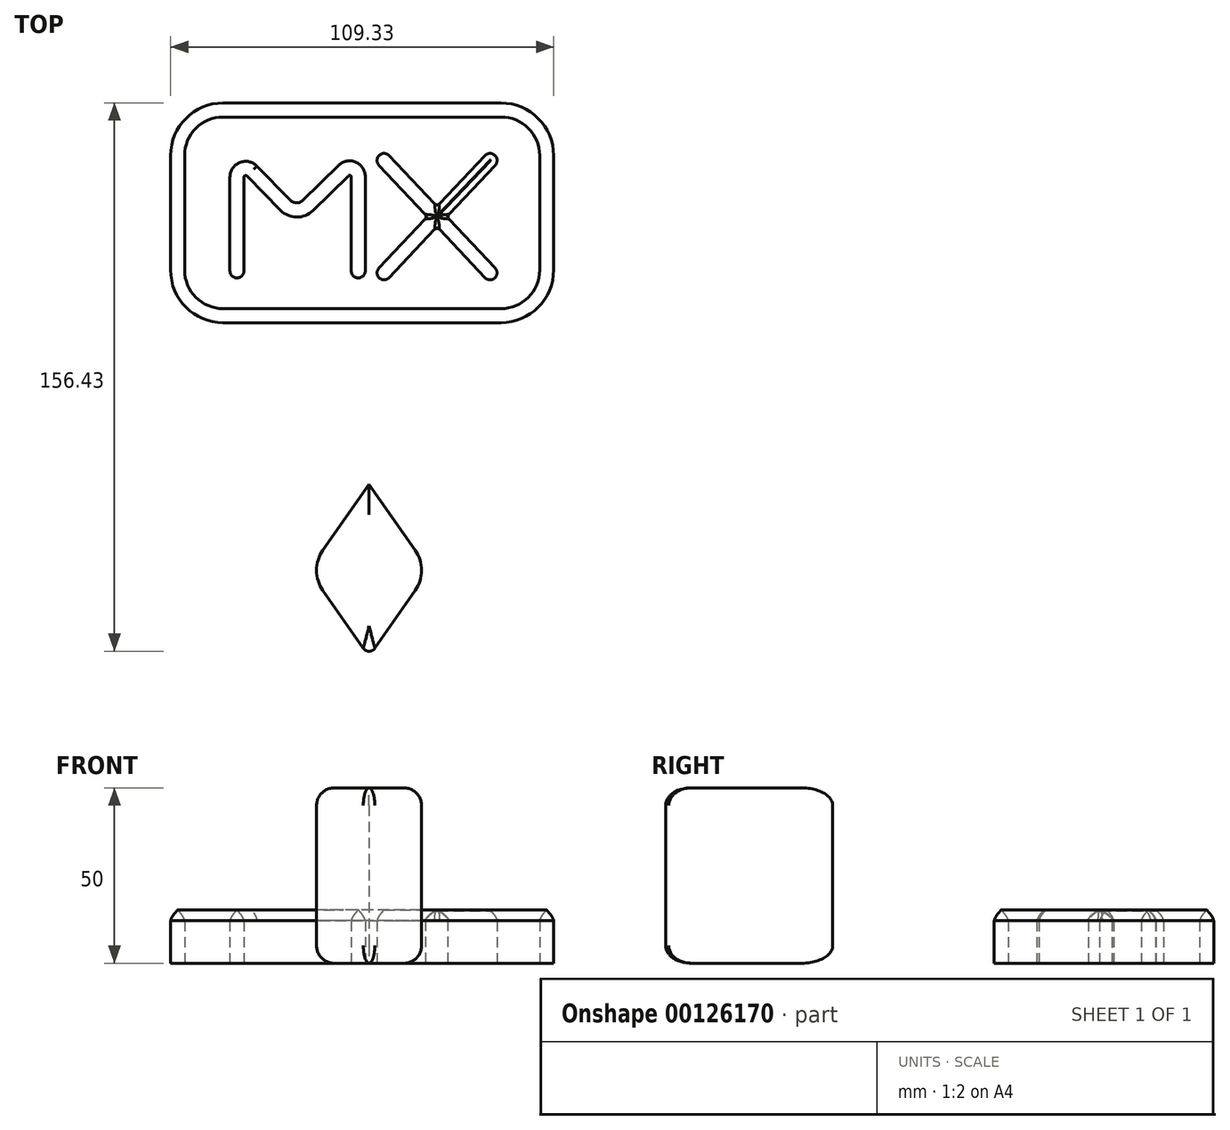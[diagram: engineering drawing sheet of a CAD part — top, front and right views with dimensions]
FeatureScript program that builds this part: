
annotation { "Feature Type Name" : "Feature", "Feature Type Description" : "" }
export const myFeature = defineFeature(function(context is Context, id is Id, definition is map)
    precondition{}
    {
        {
            var Q0;
            Q0=qCreatedBy(makeId("Top.planeOp"),FACE);
            var sketch = newSketch(context, id + "F0", { "sketchPlane" : qUnion([Q0])});
            skLineSegment(sketch, "E0.bottom", {"start": v(-41.65, 32.84) * mm, "end": v(37.68, 32.84) * mm});
            skLineSegment(sketch, "E0.top", {"start": v(-41.65, -29.83) * mm, "end": v(37.68, -29.83) * mm});
            skLineSegment(sketch, "E0.left", {"start": v(-56.65, 17.84) * mm, "end": v(-56.65, -14.83) * mm});
            skLineSegment(sketch, "E0.right", {"start": v(52.68, 17.84) * mm, "end": v(52.68, -14.83) * mm});
            skLineSegment(sketch, "E1.0", {"start": v(-41.65, 28.84) * mm, "end": v(37.68, 28.84) * mm});
            skLineSegment(sketch, "E1.1", {"start": v(-52.65, 17.84) * mm, "end": v(-52.65, -14.83) * mm});
            skLineSegment(sketch, "E1.2", {"start": v(-41.65, -25.83) * mm, "end": v(37.68, -25.83) * mm});
            skLineSegment(sketch, "E1.3", {"start": v(48.68, 17.84) * mm, "end": v(48.68, -14.83) * mm});
            skPoint(sketch, "E2.visualSharp", {"position": v(-56.65, 32.84) * mm});
            skArc(sketch, "E2.filletArc", {"start": v(-41.65, 32.84) * mm, "mid": v(-52.25, 28.45) * mm, "end": v(-56.65, 17.84) * mm});
            skPoint(sketch, "E3.visualSharp", {"position": v(-56.65, -29.83) * mm});
            skArc(sketch, "E3.filletArc", {"start": v(-56.65, -14.83) * mm, "mid": v(-52.25, -25.43) * mm, "end": v(-41.65, -29.83) * mm});
            skPoint(sketch, "E4.visualSharp", {"position": v(52.68, -29.83) * mm});
            skArc(sketch, "E4.filletArc", {"start": v(37.68, -29.83) * mm, "mid": v(48.28, -25.43) * mm, "end": v(52.68, -14.83) * mm});
            skPoint(sketch, "E5.visualSharp", {"position": v(52.68, 32.84) * mm});
            skArc(sketch, "E5.filletArc", {"start": v(52.68, 17.84) * mm, "mid": v(48.28, 28.45) * mm, "end": v(37.68, 32.84) * mm});
            skPoint(sketch, "E6.visualSharp", {"position": v(48.68, 28.84) * mm});
            skArc(sketch, "E6.filletArc", {"start": v(48.68, 17.84) * mm, "mid": v(45.45, 25.62) * mm, "end": v(37.68, 28.84) * mm});
            skPoint(sketch, "E7.visualSharp", {"position": v(48.68, -25.83) * mm});
            skArc(sketch, "E7.filletArc", {"start": v(37.68, -25.83) * mm, "mid": v(45.45, -22.6) * mm, "end": v(48.68, -14.83) * mm});
            skPoint(sketch, "E8.visualSharp", {"position": v(-52.65, -25.83) * mm});
            skArc(sketch, "E8.filletArc", {"start": v(-52.65, -14.83) * mm, "mid": v(-49.43, -22.6) * mm, "end": v(-41.65, -25.83) * mm});
            skPoint(sketch, "E9.visualSharp", {"position": v(-52.65, 28.84) * mm});
            skArc(sketch, "E9.filletArc", {"start": v(-41.65, 28.84) * mm, "mid": v(-49.43, 25.62) * mm, "end": v(-52.65, 17.84) * mm});
            skLineSegment(sketch, "E10", {"start": v(-37.72, -17.08) * mm, "end": v(-37.72, -17.08) * mm});
            skLineSegment(sketch, "E11", {"start": v(-35.72, -15.08) * mm, "end": v(-35.72, 11.7) * mm});
            skLineSegment(sketch, "E12", {"start": v(-3.08, -17.08) * mm, "end": v(-3.08, -17.08) * mm});
            skLineSegment(sketch, "E13", {"start": v(-5.08, -15.08) * mm, "end": v(-5.08, 11.73) * mm});
            skLineSegment(sketch, "E14", {"start": v(-5.93, 12.09) * mm, "end": v(-16.08, 2.15) * mm});
            skLineSegment(sketch, "E15", {"start": v(-25.27, 2.24) * mm, "end": v(-34.87, 12.04) * mm});
            skPoint(sketch, "E16.visualSharp", {"position": v(-1.08, -17.08) * mm});
            skArc(sketch, "E16.filletArc", {"start": v(-3.08, -17.08) * mm, "mid": v(-1.67, -16.5) * mm, "end": v(-1.08, -15.08) * mm});
            skPoint(sketch, "E17.visualSharp", {"position": v(-5.08, -17.08) * mm});
            skArc(sketch, "E17.filletArc", {"start": v(-5.08, -15.08) * mm, "mid": v(-4.5, -16.5) * mm, "end": v(-3.08, -17.08) * mm});
            skPoint(sketch, "E18.visualSharp", {"position": v(-35.72, -17.08) * mm});
            skArc(sketch, "E18.filletArc", {"start": v(-37.72, -17.08) * mm, "mid": v(-36.3, -16.5) * mm, "end": v(-35.72, -15.08) * mm});
            skPoint(sketch, "E19.visualSharp", {"position": v(-39.72, -17.08) * mm});
            skArc(sketch, "E19.filletArc", {"start": v(-39.72, -15.08) * mm, "mid": v(-39.14, -16.5) * mm, "end": v(-37.72, -17.08) * mm});
            skPoint(sketch, "E20.visualSharp", {"position": v(-20.73, 3.32) * mm});
            skPoint(sketch, "E21.visualSharp", {"position": v(-20.73, -2.4) * mm});
            skArc(sketch, "E21.filletArc", {"start": v(-25.27, 2.24) * mm, "mid": v(-20.7, 0.3) * mm, "end": v(-16.08, 2.15) * mm});
            skPoint(sketch, "E22.visualSharp", {"position": v(-35.72, 12.92) * mm});
            skArc(sketch, "E22.filletArc", {"start": v(-34.87, 12.04) * mm, "mid": v(-35.41, 12.16) * mm, "end": v(-35.72, 11.7) * mm});
            skPoint(sketch, "E23.visualSharp", {"position": v(-5.08, 12.92) * mm});
            skArc(sketch, "E23.filletArc", {"start": v(-5.08, 11.73) * mm, "mid": v(-5.39, 12.19) * mm, "end": v(-5.93, 12.09) * mm});
            skLineSegment(sketch, "E24", {"start": v(-39.72, 11.7) * mm, "end": v(-39.72, -15.08) * mm});
            skLineSegment(sketch, "E25", {"start": v(-1.08, 11.85) * mm, "end": v(-1.08, -15.08) * mm});
            skPoint(sketch, "E26.visualSharp", {"position": v(-39.72, 22.7) * mm});
            skArc(sketch, "E26.filletArc", {"start": v(-32, 14.84) * mm, "mid": v(-36.92, 15.86) * mm, "end": v(-39.72, 11.7) * mm});
            skArc(sketch, "E27.filletArc", {"start": v(-1.08, 11.85) * mm, "mid": v(-3.84, 16) * mm, "end": v(-8.73, 15.06) * mm});
            skLineSegment(sketch, "E28", {"start": v(-32, 14.84) * mm, "end": v(-22.48, 5.1) * mm});
            skLineSegment(sketch, "E29", {"start": v(-18.94, 5.07) * mm, "end": v(-8.73, 15.06) * mm});
            skArc(sketch, "E30.filletArc", {"start": v(-22.48, 5.1) * mm, "mid": v(-20.72, 4.35) * mm, "end": v(-18.94, 5.07) * mm});
            skLineSegment(sketch, "E31.bottom", {"start": v(2.9, 17.92) * mm, "end": v(35.9, 17.92) * mm, "construction": true});
            skLineSegment(sketch, "E31.top", {"start": v(2.9, -17.08) * mm, "end": v(35.9, -17.08) * mm, "construction": true});
            skLineSegment(sketch, "E31.left", {"start": v(2.9, 17.92) * mm, "end": v(2.9, -17.08) * mm, "construction": true});
            skLineSegment(sketch, "E31.right", {"start": v(35.9, 17.92) * mm, "end": v(35.9, -17.08) * mm, "construction": true});
            skLineSegment(sketch, "E32", {"start": v(2.9, 17.92) * mm, "end": v(2.9, 17.92) * mm});
            skLineSegment(sketch, "E33", {"start": v(35.9, -17.08) * mm, "end": v(35.9, -17.08) * mm});
            skLineSegment(sketch, "E34", {"start": v(2.9, -17.08) * mm, "end": v(2.9, -17.08) * mm});
            skLineSegment(sketch, "E35", {"start": v(35.9, 17.92) * mm, "end": v(35.9, 17.92) * mm});
            skLineSegment(sketch, "E36", {"start": v(2.82, 15.09) * mm, "end": v(33.08, -17) * mm});
            skLineSegment(sketch, "E37", {"start": v(5.73, 17.83) * mm, "end": v(35.99, -14.26) * mm});
            skLineSegment(sketch, "E38", {"start": v(33.08, 17.83) * mm, "end": v(22.1, 6.2) * mm});
            skLineSegment(sketch, "E39", {"start": v(35.99, 15.09) * mm, "end": v(25.01, 3.45) * mm});
            skPoint(sketch, "E40", {"position": v(20.73, 4.74) * mm});
            skPoint(sketch, "E41", {"position": v(23.64, 2) * mm});
            skPoint(sketch, "E42", {"position": v(15.17, -1.16) * mm});
            skPoint(sketch, "E43", {"position": v(18.08, -3.9) * mm});
            skLineSegment(sketch, "E44.trimOffspring", {"start": v(13.8, -2.62) * mm, "end": v(2.82, -14.26) * mm});
            skLineSegment(sketch, "E45.trimOffspring", {"start": v(16.7, -5.36) * mm, "end": v(5.73, -17) * mm});
            skLineSegment(sketch, "E46", {"start": v(16.62, -2.53) * mm, "end": v(16.62, -2.53) * mm});
            skLineSegment(sketch, "E47", {"start": v(22.18, 3.36) * mm, "end": v(22.18, 3.36) * mm});
            skPoint(sketch, "E48.visualSharp", {"position": v(1.45, 16.54) * mm});
            skArc(sketch, "E48.filletArc", {"start": v(2.9, 17.92) * mm, "mid": v(2.28, 16.52) * mm, "end": v(2.82, 15.09) * mm});
            skPoint(sketch, "E49.visualSharp", {"position": v(4.36, 19.29) * mm});
            skArc(sketch, "E49.filletArc", {"start": v(5.73, 17.83) * mm, "mid": v(4.33, 18.46) * mm, "end": v(2.9, 17.92) * mm});
            skPoint(sketch, "E50.visualSharp", {"position": v(37.36, -15.71) * mm});
            skArc(sketch, "E50.filletArc", {"start": v(35.9, -17.08) * mm, "mid": v(36.53, -15.69) * mm, "end": v(35.99, -14.26) * mm});
            skPoint(sketch, "E51.visualSharp", {"position": v(34.45, -18.46) * mm});
            skArc(sketch, "E51.filletArc", {"start": v(33.08, -17) * mm, "mid": v(34.47, -17.63) * mm, "end": v(35.9, -17.08) * mm});
            skArc(sketch, "E52.filletArc", {"start": v(16.62, -2.53) * mm, "mid": v(15.2, -1.99) * mm, "end": v(13.8, -2.62) * mm});
            skArc(sketch, "E53.filletArc", {"start": v(16.7, -5.36) * mm, "mid": v(17.25, -3.93) * mm, "end": v(16.62, -2.53) * mm});
            skPoint(sketch, "E54.visualSharp", {"position": v(1.45, -15.71) * mm});
            skArc(sketch, "E54.filletArc", {"start": v(2.82, -14.26) * mm, "mid": v(2.28, -15.69) * mm, "end": v(2.9, -17.08) * mm});
            skPoint(sketch, "E55.visualSharp", {"position": v(4.36, -18.46) * mm});
            skArc(sketch, "E55.filletArc", {"start": v(2.9, -17.08) * mm, "mid": v(4.33, -17.63) * mm, "end": v(5.73, -17) * mm});
            skArc(sketch, "E56.filletArc", {"start": v(22.1, 6.2) * mm, "mid": v(21.56, 4.76) * mm, "end": v(22.18, 3.36) * mm});
            skArc(sketch, "E57.filletArc", {"start": v(22.18, 3.36) * mm, "mid": v(23.61, 2.82) * mm, "end": v(25.01, 3.45) * mm});
            skPoint(sketch, "E58.visualSharp", {"position": v(34.45, 19.29) * mm});
            skArc(sketch, "E58.filletArc", {"start": v(35.9, 17.92) * mm, "mid": v(34.47, 18.46) * mm, "end": v(33.08, 17.83) * mm});
            skPoint(sketch, "E59.visualSharp", {"position": v(37.36, 16.54) * mm});
            skArc(sketch, "E59.filletArc", {"start": v(35.99, 15.09) * mm, "mid": v(36.53, 16.52) * mm, "end": v(35.9, 17.92) * mm});
            skLineSegment(sketch, "E60", {"start": v(13.8, -2.62) * mm, "end": v(22.1, 6.2) * mm});
            skLineSegment(sketch, "E61", {"start": v(16.7, -5.36) * mm, "end": v(25.01, 3.45) * mm});
            skSolve(sketch);
        }
        {
            var Q0;
            Q0=makeQuery(id+"F0.imprint","IMPRINT",FACE,{"disambiguationData":[TD([[makeQuery(id+"F0.imprint","IMPRINT",EDGE,{"derivedFrom":sQuery(id+"F0.wireOp",EDGE,"E0.bottom")}),-1.0]])]});
            var Q1;
            Q1=makeQuery(id+"F0.imprint","IMPRINT",FACE,{"disambiguationData":[TD([[makeQuery(id+"F0.imprint","IMPRINT",EDGE,{"derivedFrom":sQuery(id+"F0.wireOp",EDGE,"E11")}),1.0]])]});
            var Q2;
            {var subQ1=sQuery(id+"F0.wireOp",EDGE,"54c53401-dc7c-432c-b8d0-7c32a082aca0.filletArc");Q2=makeQuery(id+"F0.imprint","IMPRINT",FACE,{"disambiguationData":[TD([[makeQuery(id+"F0.imprint","IMPRINT",EDGE,{"derivedFrom":subQ1}),1.0]])]});}
            var Q3;
            {var subQ1=sQuery(id+"F0.wireOp",EDGE,"X9jiFzip-P22s-KY6E-eG9S-74RnpP0VEUYA");Q3=makeQuery(id+"F0.imprint","IMPRINT",FACE,{"disambiguationData":[TD([[makeQuery(id+"F0.imprint","IMPRINT",EDGE,{"derivedFrom":subQ1}),1.0]])]});}
            var Q4;
            Q4=makeQuery(id+"F0.imprint","IMPRINT",FACE,{"disambiguationData":[TD([[makeQuery(id+"F0.imprint","IMPRINT",EDGE,{"derivedFrom":sQuery(id+"F0.wireOp",EDGE,"NFEDzqPo-abMu-AeQA-jSRH-pO6B9FeDo1lR")}),-1.0]])]});
            var Q5;
            {var subQ8=sQuery(id+"F0.wireOp",EDGE,"NFEDzqPo-abMu-AeQA-jSRH-pO6B9FeDo1lR");Q5=makeQuery(id+"F0.imprint","IMPRINT",FACE,{"disambiguationData":[TD([[makeQuery(id+"F0.imprint","IMPRINT",EDGE,{"derivedFrom":subQ8}),1.0]])]});}
            var Q6;
            Q6=makeQuery(id+"F0.imprint","IMPRINT",FACE,{"disambiguationData":[TD([[makeQuery(id+"F0.imprint","IMPRINT",EDGE,{"derivedFrom":sQuery(id+"F0.wireOp",EDGE,"NFR8db7f-XhTs-96FH-58NT-pbC0jtDR2bOx")}),1.0]])]});
            var Q7;
            Q7=makeQuery(id+"F0.imprint","IMPRINT",FACE,{"disambiguationData":[TD([[makeQuery(id+"F0.imprint","IMPRINT",EDGE,{"derivedFrom":sQuery(id+"F0.wireOp",EDGE,"xYPMAhql-0Hw5-W1O3-qkBA-9yFrYDKenkE4")}),-1.0]])]});
            var Q8;
            {var subQ2=sQuery(id+"F0.wireOp",EDGE,"CNhTCM3f-eZdo-4Exa-AUP5-NEPUpIXNbu41");Q8=makeQuery(id+"F0.imprint","IMPRINT",FACE,{"disambiguationData":[TD([[makeQuery(id+"F0.imprint","IMPRINT",EDGE,{"derivedFrom":subQ2}),-1.0]])]});}
            var Q9;
            Q9=makeQuery(id+"F0.imprint","IMPRINT",FACE,{"disambiguationData":[TD([[makeQuery(id+"F0.imprint","IMPRINT",EDGE,{"derivedFrom":sQuery(id+"F0.wireOp",EDGE,"E36")}),1.0]])]});
            var Q10;
            {var subQ1=sQuery(id+"F0.wireOp",EDGE,"E48.filletArc");Q10=makeQuery(id+"F0.imprint","IMPRINT",FACE,{"disambiguationData":[TD([[makeQuery(id+"F0.imprint","IMPRINT",EDGE,{"derivedFrom":subQ1}),1.0]])]});}
            var Q11;
            {var subQ6=sQuery(id+"F0.wireOp",EDGE,"E50.filletArc");Q11=makeQuery(id+"F0.imprint","IMPRINT",FACE,{"disambiguationData":[TD([[makeQuery(id+"F0.imprint","IMPRINT",EDGE,{"derivedFrom":subQ6}),1.0]])]});}
            extrude(context, id + "F1", {"entities" : qUnion([Q0, Q1, Q2, Q3, Q4, Q5, Q6, Q7, Q8, Q9, Q10, Q11]), "depth" : 15 * mm});
        }
        {
            var Q0;
            Q0=makeQuery(id+"F0.imprint","IMPRINT",FACE,{"disambiguationData":[TD([[makeQuery(id+"F0.imprint","IMPRINT",EDGE,{"derivedFrom":sQuery(id+"F0.wireOp",EDGE,"E44.trimOffspring")}),1.0]])]});
            var Q1;
            Q1=makeQuery(id+"F0.imprint","IMPRINT",FACE,{"disambiguationData":[TD([[makeQuery(id+"F0.imprint","IMPRINT",EDGE,{"derivedFrom":sQuery(id+"F0.wireOp",EDGE,"E38")}),1.0]])]});
            var Q2;
            {var subQ1=sQuery(id+"F0.wireOp",EDGE,"E52.filletArc");Q2=makeQuery(id+"F0.imprint","IMPRINT",FACE,{"disambiguationData":[TD([[makeQuery(id+"F0.imprint","IMPRINT",EDGE,{"derivedFrom":subQ1}),-1.0]])]});}
            var Q3;
            {var subQ1=sQuery(id+"F0.wireOp",EDGE,"E56.filletArc");Q3=makeQuery(id+"F0.imprint","IMPRINT",FACE,{"disambiguationData":[TD([[makeQuery(id+"F0.imprint","IMPRINT",EDGE,{"derivedFrom":subQ1}),-1.0]])]});}
            var Q4;
            {var subQ0=sQuery(id+"F0.wireOp",EDGE,"E60");var subQ1=sQuery(id+"F0.wireOp",EDGE,"E36");var subQ2=makeQuery(id+"F0.imprint","INTERSECT",VERTEX,{"derivedFrom":[subQ1,subQ0]});Q4=makeQuery(id+"F0.imprint","IMPRINT",FACE,{"disambiguationData":[TD([[makeQuery(id+"F0.imprint","IMPRINT",EDGE,{"disambiguationData":[TD([[subQ2,-1.0]])],"derivedFrom":subQ1}),1.0]])]});}
            extrude(context, id + "F2", {"entities" : qUnion([Q0, Q1, Q2, Q3, Q4]), "depth" : 15 * mm});
        }
        {
            var Q0;
            Q0=makeQuery(id+"F1.opExtrude","CAP_FACE",FACE,{"disambiguationData":[OSD([sQuery(id+"F0.wireOp",EDGE,"E11"),sQuery(id+"F0.wireOp",EDGE,"E13"),sQuery(id+"F0.wireOp",EDGE,"E14"),sQuery(id+"F0.wireOp",EDGE,"E15"),sQuery(id+"F0.wireOp",EDGE,"E16.filletArc"),sQuery(id+"F0.wireOp",EDGE,"E17.filletArc"),sQuery(id+"F0.wireOp",EDGE,"E18.filletArc"),sQuery(id+"F0.wireOp",EDGE,"E19.filletArc"),sQuery(id+"F0.wireOp",EDGE,"E21.filletArc"),sQuery(id+"F0.wireOp",EDGE,"E22.filletArc"),sQuery(id+"F0.wireOp",EDGE,"E23.filletArc"),sQuery(id+"F0.wireOp",EDGE,"E24"),sQuery(id+"F0.wireOp",EDGE,"E25"),sQuery(id+"F0.wireOp",EDGE,"E26.filletArc"),sQuery(id+"F0.wireOp",EDGE,"E27.filletArc"),sQuery(id+"F0.wireOp",EDGE,"E28"),sQuery(id+"F0.wireOp",EDGE,"E29"),sQuery(id+"F0.wireOp",EDGE,"E30.filletArc")])],"isStart":false});
            var Q1;
            Q1=makeQuery(id+"F1.opExtrude","CAP_FACE",FACE,{"disambiguationData":[OSD([sQuery(id+"F0.wireOp",EDGE,"E0.bottom"),sQuery(id+"F0.wireOp",EDGE,"E0.top"),sQuery(id+"F0.wireOp",EDGE,"E0.left"),sQuery(id+"F0.wireOp",EDGE,"E0.right"),sQuery(id+"F0.wireOp",EDGE,"E1.0"),sQuery(id+"F0.wireOp",EDGE,"E1.1"),sQuery(id+"F0.wireOp",EDGE,"E1.2"),sQuery(id+"F0.wireOp",EDGE,"E1.3"),sQuery(id+"F0.wireOp",EDGE,"E2.filletArc"),sQuery(id+"F0.wireOp",EDGE,"E3.filletArc"),sQuery(id+"F0.wireOp",EDGE,"E4.filletArc"),sQuery(id+"F0.wireOp",EDGE,"E5.filletArc"),sQuery(id+"F0.wireOp",EDGE,"E6.filletArc"),sQuery(id+"F0.wireOp",EDGE,"E7.filletArc"),sQuery(id+"F0.wireOp",EDGE,"E8.filletArc"),sQuery(id+"F0.wireOp",EDGE,"E9.filletArc")])],"isStart":false});
            var Q2;
            Q2=makeQuery(id+"F1.opExtrude","CAP_FACE",FACE,{"disambiguationData":[OSD([sQuery(id+"F0.wireOp",EDGE,"E44.trimOffspring"),sQuery(id+"F0.wireOp",EDGE,"E45.trimOffspring"),sQuery(id+"F0.wireOp",EDGE,"E52.filletArc"),sQuery(id+"F0.wireOp",EDGE,"E53.filletArc"),sQuery(id+"F0.wireOp",EDGE,"E54.filletArc"),sQuery(id+"F0.wireOp",EDGE,"E55.filletArc")])],"isStart":false});
            var Q3;
            Q3=makeQuery(id+"F1.opExtrude","CAP_FACE",FACE,{"disambiguationData":[OSD([sQuery(id+"F0.wireOp",EDGE,"E36"),sQuery(id+"F0.wireOp",EDGE,"E37"),sQuery(id+"F0.wireOp",EDGE,"E48.filletArc"),sQuery(id+"F0.wireOp",EDGE,"E49.filletArc"),sQuery(id+"F0.wireOp",EDGE,"E50.filletArc"),sQuery(id+"F0.wireOp",EDGE,"E51.filletArc")])],"isStart":false});
            var Q4;
            Q4=makeQuery(id+"F1.opExtrude","CAP_FACE",FACE,{"disambiguationData":[OSD([sQuery(id+"F0.wireOp",EDGE,"E38"),sQuery(id+"F0.wireOp",EDGE,"E39"),sQuery(id+"F0.wireOp",EDGE,"E56.filletArc"),sQuery(id+"F0.wireOp",EDGE,"E57.filletArc"),sQuery(id+"F0.wireOp",EDGE,"E58.filletArc"),sQuery(id+"F0.wireOp",EDGE,"E59.filletArc")])],"isStart":false});
            var Q5;
            Q5=makeQuery(id+"F2.opExtrude","CAP_EDGE",EDGE,{"disambiguationData":[OSD([sQuery(id+"F0.wireOp",EDGE,"E39"),sQuery(id+"F0.wireOp",EDGE,"E45.trimOffspring"),sQuery(id+"F0.wireOp",EDGE,"E61")])],"isStart":false});
            chamfer(context, id + "F3", {"entities" : qUnion([Q0, Q1, Q2, Q3, Q4, Q5]), "width" : 1.9 * mm, "tangentPropagation" : true});
        }
        {
            var Q0;
            {var subQ0=sQuery(id+"F0.wireOp",EDGE,"E21.filletArc");Q0=makeQuery(id+"F3.opChamfer","BLEND_EDGE",EDGE,{"blendedFrom":[makeQuery(id+"F1.opExtrude","CAP_EDGE",EDGE,{"disambiguationData":[OSD([subQ0])],"isStart":false}),makeQuery(id+"F1.opExtrude","SWEPT_FACE",FACE,{"disambiguationData":[OSD([subQ0])]})],"blendedInto":[makeQuery(id+"F1.opExtrude","SWEPT_FACE",FACE,{"disambiguationData":[OSD([subQ0])]})]});}
            var Q1;
            {var subQ0=sQuery(id+"F0.wireOp",EDGE,"E0.top");Q1=makeQuery(id+"F3.opChamfer","BLEND_EDGE",EDGE,{"blendedFrom":[makeQuery(id+"F1.opExtrude","CAP_EDGE",EDGE,{"disambiguationData":[OSD([subQ0])],"isStart":false}),makeQuery(id+"F1.opExtrude","SWEPT_FACE",FACE,{"disambiguationData":[OSD([subQ0])]})],"blendedInto":[makeQuery(id+"F1.opExtrude","SWEPT_FACE",FACE,{"disambiguationData":[OSD([subQ0])]})]});}
            var Q2;
            {var subQ0=sQuery(id+"F0.wireOp",EDGE,"E1.0");Q2=makeQuery(id+"F3.opChamfer","BLEND_EDGE",EDGE,{"blendedFrom":[makeQuery(id+"F1.opExtrude","CAP_EDGE",EDGE,{"disambiguationData":[OSD([subQ0])],"isStart":false}),makeQuery(id+"F1.opExtrude","SWEPT_FACE",FACE,{"disambiguationData":[OSD([subQ0])]})],"blendedInto":[makeQuery(id+"F1.opExtrude","SWEPT_FACE",FACE,{"disambiguationData":[OSD([subQ0])]})]});}
            var Q3;
            {var subQ0=sQuery(id+"F0.wireOp",EDGE,"E45.trimOffspring");Q3=makeQuery(id+"F3.opChamfer","BLEND_EDGE",EDGE,{"blendedFrom":[makeQuery(id+"F1.opExtrude","CAP_EDGE",EDGE,{"disambiguationData":[OSD([subQ0])],"isStart":false}),makeQuery(id+"F1.opExtrude","SWEPT_FACE",FACE,{"disambiguationData":[OSD([subQ0])]})],"blendedInto":[makeQuery(id+"F1.opExtrude","SWEPT_FACE",FACE,{"disambiguationData":[OSD([subQ0])]})]});}
            var Q4;
            {var subQ0=sQuery(id+"F0.wireOp",EDGE,"E39");Q4=makeQuery(id+"F3.opChamfer","BLEND_EDGE",EDGE,{"blendedFrom":[makeQuery(id+"F1.opExtrude","CAP_EDGE",EDGE,{"disambiguationData":[OSD([subQ0])],"isStart":false}),makeQuery(id+"F1.opExtrude","SWEPT_FACE",FACE,{"disambiguationData":[OSD([subQ0])]})],"blendedInto":[makeQuery(id+"F1.opExtrude","SWEPT_FACE",FACE,{"disambiguationData":[OSD([subQ0])]})]});}
            var Q5;
            {var subQ0=sQuery(id+"F0.wireOp",EDGE,"E36");Q5=makeQuery(id+"F3.opChamfer","BLEND_EDGE",EDGE,{"blendedFrom":[makeQuery(id+"F1.opExtrude","CAP_EDGE",EDGE,{"disambiguationData":[OSD([subQ0])],"isStart":false}),makeQuery(id+"F1.opExtrude","SWEPT_FACE",FACE,{"disambiguationData":[OSD([subQ0])]})],"blendedInto":[makeQuery(id+"F1.opExtrude","SWEPT_FACE",FACE,{"disambiguationData":[OSD([subQ0])]})]});}
            var Q6;
            {var subQ0=sQuery(id+"F0.wireOp",EDGE,"E61");var subQ1=sQuery(id+"F0.wireOp",EDGE,"E45.trimOffspring");var subQ2=sQuery(id+"F0.wireOp",EDGE,"E39");Q6=makeQuery(id+"F3.opChamfer","BLEND_EDGE",EDGE,{"blendedFrom":[makeQuery(id+"F2.opExtrude","CAP_EDGE",EDGE,{"disambiguationData":[OSD([subQ2,subQ1,subQ0])],"isStart":false}),makeQuery(id+"F2.opExtrude","SWEPT_FACE",FACE,{"disambiguationData":[OSD([subQ2,subQ1,subQ0])]})],"blendedInto":[makeQuery(id+"F2.opExtrude","SWEPT_FACE",FACE,{"disambiguationData":[OSD([subQ2,subQ1,subQ0])]})]});}
            chamfer(context, id + "F4", {"entities" : qUnion([Q0, Q1, Q2, Q3, Q4, Q5, Q6]), "chamferType" : ChamferType.TWO_OFFSETS, "width1" : 1 * mm, "oppositeDirection" : false, "width2" : .6 * mm, "tangentPropagation" : true});
        }
        {
            var Q0;
            {var subQ0=sQuery(id+"F0.wireOp",EDGE,"E24");Q0=makeQuery(id+"F4.opChamfer","BLEND_EDGE",EDGE,{"blendedFrom":[makeQuery(id+"F3.opChamfer","BLEND_EDGE",EDGE,{"blendedFrom":[makeQuery(id+"F1.opExtrude","CAP_EDGE",EDGE,{"disambiguationData":[OSD([subQ0])],"isStart":false}),makeQuery(id+"F1.opExtrude","SWEPT_FACE",FACE,{"disambiguationData":[OSD([subQ0])]})],"blendedInto":[makeQuery(id+"F1.opExtrude","SWEPT_FACE",FACE,{"disambiguationData":[OSD([subQ0])]})]}),makeQuery(id+"F3.opChamfer","BLEND_FACE",FACE,{"disambiguationData":[OSD([subQ0])]})],"blendedInto":[makeQuery(id+"F3.opChamfer","BLEND_FACE",FACE,{"disambiguationData":[OSD([subQ0])]})]});}
            var Q1;
            {var subQ0=sQuery(id+"F0.wireOp",EDGE,"E0.top");Q1=makeQuery(id+"F4.opChamfer","BLEND_EDGE",EDGE,{"blendedFrom":[makeQuery(id+"F3.opChamfer","BLEND_EDGE",EDGE,{"blendedFrom":[makeQuery(id+"F1.opExtrude","CAP_EDGE",EDGE,{"disambiguationData":[OSD([subQ0])],"isStart":false}),makeQuery(id+"F1.opExtrude","SWEPT_FACE",FACE,{"disambiguationData":[OSD([subQ0])]})],"blendedInto":[makeQuery(id+"F1.opExtrude","SWEPT_FACE",FACE,{"disambiguationData":[OSD([subQ0])]})]}),makeQuery(id+"F3.opChamfer","BLEND_FACE",FACE,{"disambiguationData":[OSD([subQ0])]})],"blendedInto":[makeQuery(id+"F3.opChamfer","BLEND_FACE",FACE,{"disambiguationData":[OSD([subQ0])]})]});}
            var Q2;
            {var subQ0=sQuery(id+"F0.wireOp",EDGE,"E36");Q2=makeQuery(id+"F4.opChamfer","BLEND_EDGE",EDGE,{"blendedFrom":[makeQuery(id+"F3.opChamfer","BLEND_EDGE",EDGE,{"blendedFrom":[makeQuery(id+"F1.opExtrude","CAP_EDGE",EDGE,{"disambiguationData":[OSD([subQ0])],"isStart":false}),makeQuery(id+"F1.opExtrude","SWEPT_FACE",FACE,{"disambiguationData":[OSD([subQ0])]})],"blendedInto":[makeQuery(id+"F1.opExtrude","SWEPT_FACE",FACE,{"disambiguationData":[OSD([subQ0])]})]}),makeQuery(id+"F3.opChamfer","BLEND_FACE",FACE,{"disambiguationData":[OSD([subQ0])]})],"blendedInto":[makeQuery(id+"F3.opChamfer","BLEND_FACE",FACE,{"disambiguationData":[OSD([subQ0])]})]});}
            var Q3;
            {var subQ0=sQuery(id+"F0.wireOp",EDGE,"E45.trimOffspring");Q3=makeQuery(id+"F4.opChamfer","BLEND_EDGE",EDGE,{"blendedFrom":[makeQuery(id+"F3.opChamfer","BLEND_EDGE",EDGE,{"blendedFrom":[makeQuery(id+"F1.opExtrude","CAP_EDGE",EDGE,{"disambiguationData":[OSD([subQ0])],"isStart":false}),makeQuery(id+"F1.opExtrude","SWEPT_FACE",FACE,{"disambiguationData":[OSD([subQ0])]})],"blendedInto":[makeQuery(id+"F1.opExtrude","SWEPT_FACE",FACE,{"disambiguationData":[OSD([subQ0])]})]}),makeQuery(id+"F3.opChamfer","BLEND_FACE",FACE,{"disambiguationData":[OSD([subQ0])]})],"blendedInto":[makeQuery(id+"F3.opChamfer","BLEND_FACE",FACE,{"disambiguationData":[OSD([subQ0])]})]});}
            var Q4;
            {var subQ0=sQuery(id+"F0.wireOp",EDGE,"E39");Q4=makeQuery(id+"F4.opChamfer","BLEND_EDGE",EDGE,{"blendedFrom":[makeQuery(id+"F3.opChamfer","BLEND_EDGE",EDGE,{"blendedFrom":[makeQuery(id+"F1.opExtrude","CAP_EDGE",EDGE,{"disambiguationData":[OSD([subQ0])],"isStart":false}),makeQuery(id+"F1.opExtrude","SWEPT_FACE",FACE,{"disambiguationData":[OSD([subQ0])]})],"blendedInto":[makeQuery(id+"F1.opExtrude","SWEPT_FACE",FACE,{"disambiguationData":[OSD([subQ0])]})]}),makeQuery(id+"F3.opChamfer","BLEND_FACE",FACE,{"disambiguationData":[OSD([subQ0])]})],"blendedInto":[makeQuery(id+"F3.opChamfer","BLEND_FACE",FACE,{"disambiguationData":[OSD([subQ0])]})]});}
            var Q5;
            {var subQ0=sQuery(id+"F0.wireOp",EDGE,"E1.0");Q5=makeQuery(id+"F4.opChamfer","BLEND_EDGE",EDGE,{"blendedFrom":[makeQuery(id+"F3.opChamfer","BLEND_EDGE",EDGE,{"blendedFrom":[makeQuery(id+"F1.opExtrude","CAP_EDGE",EDGE,{"disambiguationData":[OSD([subQ0])],"isStart":false}),makeQuery(id+"F1.opExtrude","SWEPT_FACE",FACE,{"disambiguationData":[OSD([subQ0])]})],"blendedInto":[makeQuery(id+"F1.opExtrude","SWEPT_FACE",FACE,{"disambiguationData":[OSD([subQ0])]})]}),makeQuery(id+"F3.opChamfer","BLEND_FACE",FACE,{"disambiguationData":[OSD([subQ0])]})],"blendedInto":[makeQuery(id+"F3.opChamfer","BLEND_FACE",FACE,{"disambiguationData":[OSD([subQ0])]})]});}
            var Q6;
            {var subQ0=sQuery(id+"F0.wireOp",EDGE,"E61");var subQ1=sQuery(id+"F0.wireOp",EDGE,"E45.trimOffspring");var subQ2=sQuery(id+"F0.wireOp",EDGE,"E39");Q6=makeQuery(id+"F4.opChamfer","BLEND_EDGE",EDGE,{"blendedFrom":[makeQuery(id+"F3.opChamfer","BLEND_EDGE",EDGE,{"blendedFrom":[makeQuery(id+"F2.opExtrude","CAP_EDGE",EDGE,{"disambiguationData":[OSD([subQ2,subQ1,subQ0])],"isStart":false}),makeQuery(id+"F2.opExtrude","SWEPT_FACE",FACE,{"disambiguationData":[OSD([subQ2,subQ1,subQ0])]})],"blendedInto":[makeQuery(id+"F2.opExtrude","SWEPT_FACE",FACE,{"disambiguationData":[OSD([subQ2,subQ1,subQ0])]})]}),makeQuery(id+"F3.opChamfer","BLEND_FACE",FACE,{"disambiguationData":[OSD([subQ2,subQ1,subQ0])]})],"blendedInto":[makeQuery(id+"F3.opChamfer","BLEND_FACE",FACE,{"disambiguationData":[OSD([subQ2,subQ1,subQ0])]})]});}
            fillet(context, id + "F5", {"entities" : qUnion([Q0, Q1, Q2, Q3, Q4, Q5, Q6]), "radius" : 5 * mm, "tangentPropagation" : true, "allowEdgeOverflow" : false});
        }
        {
            var Q0;
            Q0=makeQuery(id+"F1.opExtrude","CAP_FACE",FACE,{"disambiguationData":[OSD([sQuery(id+"F0.wireOp",EDGE,"E11"),sQuery(id+"F0.wireOp",EDGE,"E13"),sQuery(id+"F0.wireOp",EDGE,"E14"),sQuery(id+"F0.wireOp",EDGE,"E15"),sQuery(id+"F0.wireOp",EDGE,"E16.filletArc"),sQuery(id+"F0.wireOp",EDGE,"E17.filletArc"),sQuery(id+"F0.wireOp",EDGE,"E18.filletArc"),sQuery(id+"F0.wireOp",EDGE,"E19.filletArc"),sQuery(id+"F0.wireOp",EDGE,"E21.filletArc"),sQuery(id+"F0.wireOp",EDGE,"E22.filletArc"),sQuery(id+"F0.wireOp",EDGE,"E23.filletArc"),sQuery(id+"F0.wireOp",EDGE,"E24"),sQuery(id+"F0.wireOp",EDGE,"E25"),sQuery(id+"F0.wireOp",EDGE,"E26.filletArc"),sQuery(id+"F0.wireOp",EDGE,"E27.filletArc"),sQuery(id+"F0.wireOp",EDGE,"E28"),sQuery(id+"F0.wireOp",EDGE,"E29"),sQuery(id+"F0.wireOp",EDGE,"E30.filletArc")])],"isStart":false});
            var Q1;
            Q1=makeQuery(id+"F1.opExtrude","CAP_FACE",FACE,{"disambiguationData":[OSD([sQuery(id+"F0.wireOp",EDGE,"E44.trimOffspring"),sQuery(id+"F0.wireOp",EDGE,"E45.trimOffspring"),sQuery(id+"F0.wireOp",EDGE,"E52.filletArc"),sQuery(id+"F0.wireOp",EDGE,"E53.filletArc"),sQuery(id+"F0.wireOp",EDGE,"E54.filletArc"),sQuery(id+"F0.wireOp",EDGE,"E55.filletArc")])],"isStart":false});
            var Q2;
            Q2=makeQuery(id+"F1.opExtrude","CAP_FACE",FACE,{"disambiguationData":[OSD([sQuery(id+"F0.wireOp",EDGE,"E36"),sQuery(id+"F0.wireOp",EDGE,"E37"),sQuery(id+"F0.wireOp",EDGE,"E48.filletArc"),sQuery(id+"F0.wireOp",EDGE,"E49.filletArc"),sQuery(id+"F0.wireOp",EDGE,"E50.filletArc"),sQuery(id+"F0.wireOp",EDGE,"E51.filletArc")])],"isStart":false});
            var Q3;
            Q3=makeQuery(id+"F1.opExtrude","CAP_FACE",FACE,{"disambiguationData":[OSD([sQuery(id+"F0.wireOp",EDGE,"E38"),sQuery(id+"F0.wireOp",EDGE,"E39"),sQuery(id+"F0.wireOp",EDGE,"E56.filletArc"),sQuery(id+"F0.wireOp",EDGE,"E57.filletArc"),sQuery(id+"F0.wireOp",EDGE,"E58.filletArc"),sQuery(id+"F0.wireOp",EDGE,"E59.filletArc")])],"isStart":false});
            var Q4;
            Q4=makeQuery(id+"F1.opExtrude","CAP_FACE",FACE,{"disambiguationData":[OSD([sQuery(id+"F0.wireOp",EDGE,"E0.bottom"),sQuery(id+"F0.wireOp",EDGE,"E0.top"),sQuery(id+"F0.wireOp",EDGE,"E0.left"),sQuery(id+"F0.wireOp",EDGE,"E0.right"),sQuery(id+"F0.wireOp",EDGE,"E1.0"),sQuery(id+"F0.wireOp",EDGE,"E1.1"),sQuery(id+"F0.wireOp",EDGE,"E1.2"),sQuery(id+"F0.wireOp",EDGE,"E1.3"),sQuery(id+"F0.wireOp",EDGE,"E2.filletArc"),sQuery(id+"F0.wireOp",EDGE,"E3.filletArc"),sQuery(id+"F0.wireOp",EDGE,"E4.filletArc"),sQuery(id+"F0.wireOp",EDGE,"E5.filletArc"),sQuery(id+"F0.wireOp",EDGE,"E6.filletArc"),sQuery(id+"F0.wireOp",EDGE,"E7.filletArc"),sQuery(id+"F0.wireOp",EDGE,"E8.filletArc"),sQuery(id+"F0.wireOp",EDGE,"E9.filletArc")])],"isStart":false});
            var Q5;
            Q5=makeQuery(id+"F2.opExtrude","CAP_FACE",FACE,{"disambiguationData":[OSD([sQuery(id+"F0.wireOp",EDGE,"E38"),sQuery(id+"F0.wireOp",EDGE,"E39"),sQuery(id+"F0.wireOp",EDGE,"E44.trimOffspring"),sQuery(id+"F0.wireOp",EDGE,"E45.trimOffspring"),sQuery(id+"F0.wireOp",EDGE,"E54.filletArc"),sQuery(id+"F0.wireOp",EDGE,"E55.filletArc"),sQuery(id+"F0.wireOp",EDGE,"E58.filletArc"),sQuery(id+"F0.wireOp",EDGE,"E59.filletArc"),sQuery(id+"F0.wireOp",EDGE,"E60"),sQuery(id+"F0.wireOp",EDGE,"E61")])],"isStart":false});
            extrude(context, id + "F6", {"entities" : qUnion([Q0, Q1, Q2, Q3, Q4, Q5]), "operationType" : NewBodyOperationType.ADD, "depth" : .2 * mm});
        }
        {
            var Q0;
            {var subQ0=sQuery(id+"F0.wireOp",EDGE,"E9.filletArc");var subQ1=sQuery(id+"F0.wireOp",EDGE,"E8.filletArc");var subQ2=sQuery(id+"F0.wireOp",EDGE,"E7.filletArc");var subQ3=sQuery(id+"F0.wireOp",EDGE,"E6.filletArc");var subQ4=sQuery(id+"F0.wireOp",EDGE,"E5.filletArc");var subQ5=sQuery(id+"F0.wireOp",EDGE,"E4.filletArc");var subQ6=sQuery(id+"F0.wireOp",EDGE,"E3.filletArc");var subQ7=sQuery(id+"F0.wireOp",EDGE,"E2.filletArc");var subQ8=sQuery(id+"F0.wireOp",EDGE,"E1.3");var subQ9=sQuery(id+"F0.wireOp",EDGE,"E1.2");var subQ10=sQuery(id+"F0.wireOp",EDGE,"E1.1");var subQ11=sQuery(id+"F0.wireOp",EDGE,"E1.0");var subQ12=sQuery(id+"F0.wireOp",EDGE,"E0.right");var subQ13=sQuery(id+"F0.wireOp",EDGE,"E0.left");var subQ14=sQuery(id+"F0.wireOp",EDGE,"E0.top");var subQ15=sQuery(id+"F0.wireOp",EDGE,"E0.bottom");var subQ16=makeQuery(id+"F3.opChamfer","BLEND_EDGE",EDGE,{"blendedFrom":[makeQuery(id+"F1.opExtrude","CAP_EDGE",EDGE,{"disambiguationData":[OSD([subQ14])],"isStart":false}),makeQuery(id+"F1.opExtrude","CAP_FACE",FACE,{"disambiguationData":[OSD([subQ15,subQ14,subQ13,subQ12,subQ11,subQ10,subQ9,subQ8,subQ7,subQ6,subQ5,subQ4,subQ3,subQ2,subQ1,subQ0])],"isStart":false})],"blendedInto":[makeQuery(id+"F1.opExtrude","CAP_FACE",FACE,{"disambiguationData":[OSD([subQ15,subQ14,subQ13,subQ12,subQ11,subQ10,subQ9,subQ8,subQ7,subQ6,subQ5,subQ4,subQ3,subQ2,subQ1,subQ0])],"isStart":false})]});Q0=makeQuery(id+"F6.boolean.opBoolean","MERGE",EDGE,{"derivedFrom":[subQ16,makeQuery(id+"F6.opExtrude","CAP_EDGE",EDGE,{"disambiguationData":[OSD([subQ15,subQ14,subQ13,subQ12,subQ11,subQ10,subQ9,subQ8,subQ7,subQ6,subQ5,subQ4,subQ3,subQ2,subQ1,subQ0]),TDD([subQ16])],"isStart":true})]});}
            var Q1;
            {var subQ0=sQuery(id+"F0.wireOp",EDGE,"E55.filletArc");var subQ1=sQuery(id+"F0.wireOp",EDGE,"E54.filletArc");var subQ2=sQuery(id+"F0.wireOp",EDGE,"E53.filletArc");var subQ3=sQuery(id+"F0.wireOp",EDGE,"E52.filletArc");var subQ4=sQuery(id+"F0.wireOp",EDGE,"E45.trimOffspring");var subQ5=sQuery(id+"F0.wireOp",EDGE,"E44.trimOffspring");var subQ6=makeQuery(id+"F3.opChamfer","BLEND_EDGE",EDGE,{"blendedFrom":[makeQuery(id+"F1.opExtrude","CAP_EDGE",EDGE,{"disambiguationData":[OSD([subQ4])],"isStart":false}),makeQuery(id+"F1.opExtrude","CAP_FACE",FACE,{"disambiguationData":[OSD([subQ5,subQ4,subQ3,subQ2,subQ1,subQ0])],"isStart":false})],"blendedInto":[makeQuery(id+"F1.opExtrude","CAP_FACE",FACE,{"disambiguationData":[OSD([subQ5,subQ4,subQ3,subQ2,subQ1,subQ0])],"isStart":false})]});Q1=makeQuery(id+"F6.boolean.opBoolean","MERGE",EDGE,{"derivedFrom":[subQ6,makeQuery(id+"F6.opExtrude","CAP_EDGE",EDGE,{"disambiguationData":[OSD([subQ5,subQ4,subQ3,subQ2,subQ1,subQ0]),TDD([subQ6])],"isStart":true})]});}
            var Q2;
            {var subQ0=sQuery(id+"F0.wireOp",EDGE,"E30.filletArc");var subQ1=sQuery(id+"F0.wireOp",EDGE,"E29");var subQ2=sQuery(id+"F0.wireOp",EDGE,"E28");var subQ3=sQuery(id+"F0.wireOp",EDGE,"E27.filletArc");var subQ4=sQuery(id+"F0.wireOp",EDGE,"E26.filletArc");var subQ5=sQuery(id+"F0.wireOp",EDGE,"E25");var subQ6=sQuery(id+"F0.wireOp",EDGE,"E24");var subQ7=sQuery(id+"F0.wireOp",EDGE,"E23.filletArc");var subQ8=sQuery(id+"F0.wireOp",EDGE,"E22.filletArc");var subQ9=sQuery(id+"F0.wireOp",EDGE,"E21.filletArc");var subQ10=sQuery(id+"F0.wireOp",EDGE,"E19.filletArc");var subQ11=sQuery(id+"F0.wireOp",EDGE,"E18.filletArc");var subQ12=sQuery(id+"F0.wireOp",EDGE,"E17.filletArc");var subQ13=sQuery(id+"F0.wireOp",EDGE,"E16.filletArc");var subQ14=sQuery(id+"F0.wireOp",EDGE,"E15");var subQ15=sQuery(id+"F0.wireOp",EDGE,"E14");var subQ16=sQuery(id+"F0.wireOp",EDGE,"E13");var subQ17=sQuery(id+"F0.wireOp",EDGE,"E11");var subQ18=makeQuery(id+"F3.opChamfer","BLEND_EDGE",EDGE,{"blendedFrom":[makeQuery(id+"F1.opExtrude","CAP_EDGE",EDGE,{"disambiguationData":[OSD([subQ16])],"isStart":false}),makeQuery(id+"F1.opExtrude","CAP_FACE",FACE,{"disambiguationData":[OSD([subQ17,subQ16,subQ15,subQ14,subQ13,subQ12,subQ11,subQ10,subQ9,subQ8,subQ7,subQ6,subQ5,subQ4,subQ3,subQ2,subQ1,subQ0])],"isStart":false})],"blendedInto":[makeQuery(id+"F1.opExtrude","CAP_FACE",FACE,{"disambiguationData":[OSD([subQ17,subQ16,subQ15,subQ14,subQ13,subQ12,subQ11,subQ10,subQ9,subQ8,subQ7,subQ6,subQ5,subQ4,subQ3,subQ2,subQ1,subQ0])],"isStart":false})]});Q2=makeQuery(id+"F6.boolean.opBoolean","MERGE",EDGE,{"derivedFrom":[subQ18,makeQuery(id+"F6.opExtrude","CAP_EDGE",EDGE,{"disambiguationData":[OSD([subQ17,subQ16,subQ15,subQ14,subQ13,subQ12,subQ11,subQ10,subQ9,subQ8,subQ7,subQ6,subQ5,subQ4,subQ3,subQ2,subQ1,subQ0]),TDD([subQ18])],"isStart":true})]});}
            var Q3;
            {var subQ0=sQuery(id+"F0.wireOp",EDGE,"E51.filletArc");var subQ1=sQuery(id+"F0.wireOp",EDGE,"E50.filletArc");var subQ2=sQuery(id+"F0.wireOp",EDGE,"E49.filletArc");var subQ3=sQuery(id+"F0.wireOp",EDGE,"E48.filletArc");var subQ4=sQuery(id+"F0.wireOp",EDGE,"E37");var subQ5=sQuery(id+"F0.wireOp",EDGE,"E36");var subQ6=makeQuery(id+"F3.opChamfer","BLEND_EDGE",EDGE,{"blendedFrom":[makeQuery(id+"F1.opExtrude","CAP_EDGE",EDGE,{"disambiguationData":[OSD([subQ5])],"isStart":false}),makeQuery(id+"F1.opExtrude","CAP_FACE",FACE,{"disambiguationData":[OSD([subQ5,subQ4,subQ3,subQ2,subQ1,subQ0])],"isStart":false})],"blendedInto":[makeQuery(id+"F1.opExtrude","CAP_FACE",FACE,{"disambiguationData":[OSD([subQ5,subQ4,subQ3,subQ2,subQ1,subQ0])],"isStart":false})]});Q3=makeQuery(id+"F6.boolean.opBoolean","MERGE",EDGE,{"derivedFrom":[subQ6,makeQuery(id+"F6.opExtrude","CAP_EDGE",EDGE,{"disambiguationData":[OSD([subQ5,subQ4,subQ3,subQ2,subQ1,subQ0]),TDD([subQ6])],"isStart":true})]});}
            var Q4;
            {var subQ0=sQuery(id+"F0.wireOp",EDGE,"E59.filletArc");var subQ1=sQuery(id+"F0.wireOp",EDGE,"E58.filletArc");var subQ2=sQuery(id+"F0.wireOp",EDGE,"E57.filletArc");var subQ3=sQuery(id+"F0.wireOp",EDGE,"E56.filletArc");var subQ4=sQuery(id+"F0.wireOp",EDGE,"E39");var subQ5=sQuery(id+"F0.wireOp",EDGE,"E38");var subQ6=makeQuery(id+"F3.opChamfer","BLEND_EDGE",EDGE,{"blendedFrom":[makeQuery(id+"F1.opExtrude","CAP_EDGE",EDGE,{"disambiguationData":[OSD([subQ4])],"isStart":false}),makeQuery(id+"F1.opExtrude","CAP_FACE",FACE,{"disambiguationData":[OSD([subQ5,subQ4,subQ3,subQ2,subQ1,subQ0])],"isStart":false})],"blendedInto":[makeQuery(id+"F1.opExtrude","CAP_FACE",FACE,{"disambiguationData":[OSD([subQ5,subQ4,subQ3,subQ2,subQ1,subQ0])],"isStart":false})]});Q4=makeQuery(id+"F6.boolean.opBoolean","MERGE",EDGE,{"derivedFrom":[subQ6,makeQuery(id+"F6.opExtrude","CAP_EDGE",EDGE,{"disambiguationData":[OSD([subQ5,subQ4,subQ3,subQ2,subQ1,subQ0]),TDD([subQ6])],"isStart":true})]});}
            var Q5;
            {var subQ0=sQuery(id+"F0.wireOp",EDGE,"E9.filletArc");var subQ1=sQuery(id+"F0.wireOp",EDGE,"E8.filletArc");var subQ2=sQuery(id+"F0.wireOp",EDGE,"E7.filletArc");var subQ3=sQuery(id+"F0.wireOp",EDGE,"E6.filletArc");var subQ4=sQuery(id+"F0.wireOp",EDGE,"E5.filletArc");var subQ5=sQuery(id+"F0.wireOp",EDGE,"E4.filletArc");var subQ6=sQuery(id+"F0.wireOp",EDGE,"E3.filletArc");var subQ7=sQuery(id+"F0.wireOp",EDGE,"E2.filletArc");var subQ8=sQuery(id+"F0.wireOp",EDGE,"E1.3");var subQ9=sQuery(id+"F0.wireOp",EDGE,"E1.2");var subQ10=sQuery(id+"F0.wireOp",EDGE,"E1.1");var subQ11=sQuery(id+"F0.wireOp",EDGE,"E1.0");var subQ12=sQuery(id+"F0.wireOp",EDGE,"E0.right");var subQ13=sQuery(id+"F0.wireOp",EDGE,"E0.left");var subQ14=sQuery(id+"F0.wireOp",EDGE,"E0.top");var subQ15=sQuery(id+"F0.wireOp",EDGE,"E0.bottom");var subQ16=makeQuery(id+"F3.opChamfer","BLEND_EDGE",EDGE,{"blendedFrom":[makeQuery(id+"F1.opExtrude","CAP_EDGE",EDGE,{"disambiguationData":[OSD([subQ11])],"isStart":false}),makeQuery(id+"F1.opExtrude","CAP_FACE",FACE,{"disambiguationData":[OSD([subQ15,subQ14,subQ13,subQ12,subQ11,subQ10,subQ9,subQ8,subQ7,subQ6,subQ5,subQ4,subQ3,subQ2,subQ1,subQ0])],"isStart":false})],"blendedInto":[makeQuery(id+"F1.opExtrude","CAP_FACE",FACE,{"disambiguationData":[OSD([subQ15,subQ14,subQ13,subQ12,subQ11,subQ10,subQ9,subQ8,subQ7,subQ6,subQ5,subQ4,subQ3,subQ2,subQ1,subQ0])],"isStart":false})]});Q5=makeQuery(id+"F6.boolean.opBoolean","MERGE",EDGE,{"derivedFrom":[subQ16,makeQuery(id+"F6.opExtrude","CAP_EDGE",EDGE,{"disambiguationData":[OSD([subQ15,subQ14,subQ13,subQ12,subQ11,subQ10,subQ9,subQ8,subQ7,subQ6,subQ5,subQ4,subQ3,subQ2,subQ1,subQ0]),TDD([subQ16])],"isStart":true})]});}
            var Q6;
            {var subQ0=sQuery(id+"F0.wireOp",EDGE,"E61");var subQ1=sQuery(id+"F0.wireOp",EDGE,"E60");var subQ2=sQuery(id+"F0.wireOp",EDGE,"E59.filletArc");var subQ3=sQuery(id+"F0.wireOp",EDGE,"E58.filletArc");var subQ4=sQuery(id+"F0.wireOp",EDGE,"E55.filletArc");var subQ5=sQuery(id+"F0.wireOp",EDGE,"E54.filletArc");var subQ6=sQuery(id+"F0.wireOp",EDGE,"E45.trimOffspring");var subQ7=sQuery(id+"F0.wireOp",EDGE,"E44.trimOffspring");var subQ8=sQuery(id+"F0.wireOp",EDGE,"E39");var subQ9=sQuery(id+"F0.wireOp",EDGE,"E38");var subQ10=makeQuery(id+"F3.opChamfer","BLEND_EDGE",EDGE,{"blendedFrom":[makeQuery(id+"F2.opExtrude","CAP_EDGE",EDGE,{"disambiguationData":[OSD([subQ8,subQ6,subQ0])],"isStart":false}),makeQuery(id+"F2.opExtrude","CAP_FACE",FACE,{"disambiguationData":[OSD([subQ9,subQ8,subQ7,subQ6,subQ5,subQ4,subQ3,subQ2,subQ1,subQ0])],"isStart":false})],"blendedInto":[makeQuery(id+"F2.opExtrude","CAP_FACE",FACE,{"disambiguationData":[OSD([subQ9,subQ8,subQ7,subQ6,subQ5,subQ4,subQ3,subQ2,subQ1,subQ0])],"isStart":false})]});Q6=makeQuery(id+"F6.boolean.opBoolean","MERGE",EDGE,{"disambiguationData":[OD(0.0)],"derivedFrom":[subQ10,makeQuery(id+"F6.opExtrude","CAP_EDGE",EDGE,{"disambiguationData":[OSD([subQ9,subQ8,subQ7,subQ6,subQ5,subQ4,subQ3,subQ2,subQ1,subQ0]),TDD([subQ10])],"isStart":true})]});}
            fillet(context, id + "F7", {"entities" : qUnion([Q0, Q1, Q2, Q3, Q4, Q5, Q6]), "radius" : 2 * mm, "tangentPropagation" : true, "allowEdgeOverflow" : false});
        }
        {
            var Q0;
            Q0=makeQuery(id+"F6.opExtrude","CAP_FACE",FACE,{"disambiguationData":[OSD([sQuery(id+"F0.wireOp",EDGE,"E11"),sQuery(id+"F0.wireOp",EDGE,"E13"),sQuery(id+"F0.wireOp",EDGE,"E14"),sQuery(id+"F0.wireOp",EDGE,"E15"),sQuery(id+"F0.wireOp",EDGE,"E16.filletArc"),sQuery(id+"F0.wireOp",EDGE,"E17.filletArc"),sQuery(id+"F0.wireOp",EDGE,"E18.filletArc"),sQuery(id+"F0.wireOp",EDGE,"E19.filletArc"),sQuery(id+"F0.wireOp",EDGE,"E21.filletArc"),sQuery(id+"F0.wireOp",EDGE,"E22.filletArc"),sQuery(id+"F0.wireOp",EDGE,"E23.filletArc"),sQuery(id+"F0.wireOp",EDGE,"E24"),sQuery(id+"F0.wireOp",EDGE,"E25"),sQuery(id+"F0.wireOp",EDGE,"E26.filletArc"),sQuery(id+"F0.wireOp",EDGE,"E27.filletArc"),sQuery(id+"F0.wireOp",EDGE,"E28"),sQuery(id+"F0.wireOp",EDGE,"E29"),sQuery(id+"F0.wireOp",EDGE,"E30.filletArc")])],"isStart":false});
            var Q1;
            Q1=makeQuery(id+"F6.opExtrude","CAP_FACE",FACE,{"disambiguationData":[OSD([sQuery(id+"F0.wireOp",EDGE,"E44.trimOffspring"),sQuery(id+"F0.wireOp",EDGE,"E45.trimOffspring"),sQuery(id+"F0.wireOp",EDGE,"E52.filletArc"),sQuery(id+"F0.wireOp",EDGE,"E53.filletArc"),sQuery(id+"F0.wireOp",EDGE,"E54.filletArc"),sQuery(id+"F0.wireOp",EDGE,"E55.filletArc")])],"isStart":false});
            var Q2;
            Q2=makeQuery(id+"F6.opExtrude","CAP_FACE",FACE,{"disambiguationData":[OSD([sQuery(id+"F0.wireOp",EDGE,"E0.bottom"),sQuery(id+"F0.wireOp",EDGE,"E0.top"),sQuery(id+"F0.wireOp",EDGE,"E0.left"),sQuery(id+"F0.wireOp",EDGE,"E0.right"),sQuery(id+"F0.wireOp",EDGE,"E1.0"),sQuery(id+"F0.wireOp",EDGE,"E1.1"),sQuery(id+"F0.wireOp",EDGE,"E1.2"),sQuery(id+"F0.wireOp",EDGE,"E1.3"),sQuery(id+"F0.wireOp",EDGE,"E2.filletArc"),sQuery(id+"F0.wireOp",EDGE,"E3.filletArc"),sQuery(id+"F0.wireOp",EDGE,"E4.filletArc"),sQuery(id+"F0.wireOp",EDGE,"E5.filletArc"),sQuery(id+"F0.wireOp",EDGE,"E6.filletArc"),sQuery(id+"F0.wireOp",EDGE,"E7.filletArc"),sQuery(id+"F0.wireOp",EDGE,"E8.filletArc"),sQuery(id+"F0.wireOp",EDGE,"E9.filletArc")])],"isStart":false});
            var Q3;
            Q3=makeQuery(id+"F6.opExtrude","CAP_FACE",FACE,{"disambiguationData":[OSD([sQuery(id+"F0.wireOp",EDGE,"E36"),sQuery(id+"F0.wireOp",EDGE,"E37"),sQuery(id+"F0.wireOp",EDGE,"E48.filletArc"),sQuery(id+"F0.wireOp",EDGE,"E49.filletArc"),sQuery(id+"F0.wireOp",EDGE,"E50.filletArc"),sQuery(id+"F0.wireOp",EDGE,"E51.filletArc")])],"isStart":false});
            var Q4;
            Q4=makeQuery(id+"F6.opExtrude","CAP_FACE",FACE,{"disambiguationData":[OSD([sQuery(id+"F0.wireOp",EDGE,"E38"),sQuery(id+"F0.wireOp",EDGE,"E39"),sQuery(id+"F0.wireOp",EDGE,"E56.filletArc"),sQuery(id+"F0.wireOp",EDGE,"E57.filletArc"),sQuery(id+"F0.wireOp",EDGE,"E58.filletArc"),sQuery(id+"F0.wireOp",EDGE,"E59.filletArc")])],"isStart":false});
            fillet(context, id + "F8", {"entities" : qUnion([Q0, Q1, Q2, Q3, Q4]), "radius" : .1 * mm, "tangentPropagation" : true, "allowEdgeOverflow" : false});
        }
        {
            var Q0;
            Q0=makeQuery(id+"F6.boolean.opBoolean","INTERSECT",EDGE,{"derivedFrom":[makeQuery(id+"F1.opExtrude","SWEPT_FACE",FACE,{"disambiguationData":[OSD([sQuery(id+"F0.wireOp",EDGE,"E36")])]}),makeQuery(id+"F2.opExtrude","SWEPT_FACE",FACE,{"disambiguationData":[OSD([sQuery(id+"F0.wireOp",EDGE,"E39"),sQuery(id+"F0.wireOp",EDGE,"E45.trimOffspring"),sQuery(id+"F0.wireOp",EDGE,"E61")])]})]});
            var Q1;
            Q1=makeQuery(id+"F6.boolean.opBoolean","INTERSECT",EDGE,{"derivedFrom":[makeQuery(id+"F4.opChamfer","BLEND_FACE",FACE,{"disambiguationData":[OSD([sQuery(id+"F0.wireOp",EDGE,"E36")])]}),makeQuery(id+"F4.opChamfer","BLEND_FACE",FACE,{"disambiguationData":[OSD([sQuery(id+"F0.wireOp",EDGE,"E39"),sQuery(id+"F0.wireOp",EDGE,"E45.trimOffspring"),sQuery(id+"F0.wireOp",EDGE,"E61")])]})]});
            var Q2;
            Q2=makeQuery(id+"F6.boolean.opBoolean","INTERSECT",EDGE,{"derivedFrom":[makeQuery(id+"F5.opFillet","BLEND_FACE",FACE,{"disambiguationData":[OSD([sQuery(id+"F0.wireOp",EDGE,"E36")])]}),makeQuery(id+"F5.opFillet","BLEND_FACE",FACE,{"disambiguationData":[OSD([sQuery(id+"F0.wireOp",EDGE,"E39"),sQuery(id+"F0.wireOp",EDGE,"E45.trimOffspring"),sQuery(id+"F0.wireOp",EDGE,"E61")])]})]});
            var Q3;
            Q3=makeQuery(id+"F6.boolean.opBoolean","INTERSECT",EDGE,{"derivedFrom":[makeQuery(id+"F1.opExtrude","SWEPT_FACE",FACE,{"disambiguationData":[OSD([sQuery(id+"F0.wireOp",EDGE,"E37")])]}),makeQuery(id+"F2.opExtrude","SWEPT_FACE",FACE,{"disambiguationData":[OSD([sQuery(id+"F0.wireOp",EDGE,"E39"),sQuery(id+"F0.wireOp",EDGE,"E45.trimOffspring"),sQuery(id+"F0.wireOp",EDGE,"E61")])]})]});
            var Q4;
            Q4=makeQuery(id+"F6.boolean.opBoolean","INTERSECT",EDGE,{"derivedFrom":[makeQuery(id+"F4.opChamfer","BLEND_FACE",FACE,{"disambiguationData":[OSD([sQuery(id+"F0.wireOp",EDGE,"E37")])]}),makeQuery(id+"F4.opChamfer","BLEND_FACE",FACE,{"disambiguationData":[OSD([sQuery(id+"F0.wireOp",EDGE,"E39"),sQuery(id+"F0.wireOp",EDGE,"E45.trimOffspring"),sQuery(id+"F0.wireOp",EDGE,"E61")])]})]});
            var Q5;
            Q5=makeQuery(id+"F6.boolean.opBoolean","INTERSECT",EDGE,{"derivedFrom":[makeQuery(id+"F5.opFillet","BLEND_FACE",FACE,{"disambiguationData":[OSD([sQuery(id+"F0.wireOp",EDGE,"E37")])]}),makeQuery(id+"F5.opFillet","BLEND_FACE",FACE,{"disambiguationData":[OSD([sQuery(id+"F0.wireOp",EDGE,"E39"),sQuery(id+"F0.wireOp",EDGE,"E45.trimOffspring"),sQuery(id+"F0.wireOp",EDGE,"E61")])]})]});
            var Q6;
            Q6=makeQuery(id+"F6.boolean.opBoolean","INTERSECT",EDGE,{"derivedFrom":[makeQuery(id+"F1.opExtrude","SWEPT_FACE",FACE,{"disambiguationData":[OSD([sQuery(id+"F0.wireOp",EDGE,"E37")])]}),makeQuery(id+"F2.opExtrude","SWEPT_FACE",FACE,{"disambiguationData":[OSD([sQuery(id+"F0.wireOp",EDGE,"E38"),sQuery(id+"F0.wireOp",EDGE,"E44.trimOffspring"),sQuery(id+"F0.wireOp",EDGE,"E60")])]})]});
            var Q7;
            Q7=makeQuery(id+"F6.boolean.opBoolean","INTERSECT",EDGE,{"derivedFrom":[makeQuery(id+"F4.opChamfer","BLEND_FACE",FACE,{"disambiguationData":[OSD([sQuery(id+"F0.wireOp",EDGE,"E37")])]}),makeQuery(id+"F4.opChamfer","BLEND_FACE",FACE,{"disambiguationData":[OSD([sQuery(id+"F0.wireOp",EDGE,"E38"),sQuery(id+"F0.wireOp",EDGE,"E44.trimOffspring"),sQuery(id+"F0.wireOp",EDGE,"E60")])]})]});
            var Q8;
            Q8=makeQuery(id+"F6.boolean.opBoolean","INTERSECT",EDGE,{"derivedFrom":[makeQuery(id+"F1.opExtrude","SWEPT_FACE",FACE,{"disambiguationData":[OSD([sQuery(id+"F0.wireOp",EDGE,"E36")])]}),makeQuery(id+"F2.opExtrude","SWEPT_FACE",FACE,{"disambiguationData":[OSD([sQuery(id+"F0.wireOp",EDGE,"E38"),sQuery(id+"F0.wireOp",EDGE,"E44.trimOffspring"),sQuery(id+"F0.wireOp",EDGE,"E60")])]})]});
            var Q9;
            Q9=makeQuery(id+"F6.boolean.opBoolean","INTERSECT",EDGE,{"derivedFrom":[makeQuery(id+"F4.opChamfer","BLEND_FACE",FACE,{"disambiguationData":[OSD([sQuery(id+"F0.wireOp",EDGE,"E36")])]}),makeQuery(id+"F4.opChamfer","BLEND_FACE",FACE,{"disambiguationData":[OSD([sQuery(id+"F0.wireOp",EDGE,"E38"),sQuery(id+"F0.wireOp",EDGE,"E44.trimOffspring"),sQuery(id+"F0.wireOp",EDGE,"E60")])]})]});
            var Q10;
            Q10=makeQuery(id+"F6.boolean.opBoolean","INTERSECT",EDGE,{"derivedFrom":[makeQuery(id+"F5.opFillet","BLEND_FACE",FACE,{"disambiguationData":[OSD([sQuery(id+"F0.wireOp",EDGE,"E36")])]}),makeQuery(id+"F5.opFillet","BLEND_FACE",FACE,{"disambiguationData":[OSD([sQuery(id+"F0.wireOp",EDGE,"E38"),sQuery(id+"F0.wireOp",EDGE,"E44.trimOffspring"),sQuery(id+"F0.wireOp",EDGE,"E60")])]})]});
            fillet(context, id + "F9", {"entities" : qUnion([Q0, Q1, Q2, Q3, Q4, Q5, Q6, Q7, Q8, Q9, Q10]), "radius" : 1 * mm, "allowEdgeOverflow" : false});
        }
        {
            var Q0;
            Q0=qCreatedBy(makeId("Top.planeOp"),FACE);
            var sketch = newSketch(context, id + "F10", { "sketchPlane" : qUnion([Q0])});
            skLineSegment(sketch, "E62", {"start": v(0, -75.93) * mm, "end": v(-13.2, -94.77) * mm});
            skLineSegment(sketch, "E63", {"start": v(-13.2, -106.24) * mm, "end": v(-1.64, -122.74) * mm});
            skLineSegment(sketch, "E64", {"start": v(1.64, -122.74) * mm, "end": v(13.2, -106.24) * mm});
            skLineSegment(sketch, "E65", {"start": v(13.2, -94.77) * mm, "end": v(0, -75.93) * mm});
            skLineSegment(sketch, "E66", {"start": v(-17.2, -100.5) * mm, "end": v(17.2, -100.5) * mm});
            skPoint(sketch, "E67", {"position": v(0, -100.5) * mm});
            skPoint(sketch, "E68.visualSharp", {"position": v(-17.2, -100.5) * mm});
            skArc(sketch, "E68.filletArc", {"start": v(-13.2, -94.77) * mm, "mid": v(-15, -100.5) * mm, "end": v(-13.2, -106.24) * mm});
            skPoint(sketch, "E69.visualSharp", {"position": v(17.2, -100.5) * mm});
            skArc(sketch, "E69.filletArc", {"start": v(13.2, -106.24) * mm, "mid": v(15, -100.5) * mm, "end": v(13.2, -94.77) * mm});
            skPoint(sketch, "E70.visualSharp", {"position": v(0, -125.08) * mm});
            skArc(sketch, "E70.filletArc", {"start": v(-1.64, -122.74) * mm, "mid": v(0, -123.6) * mm, "end": v(1.64, -122.74) * mm});
            skSolve(sketch);
        }
        {
            var Q0;
            Q0 = qSketchRegion(id + "F10", true);
            extrude(context, id + "F11", {"entities" : qUnion([Q0]), "depth" : 50 * mm});
        }
        {
            var Q0;
            Q0=makeQuery(id+"F11.opExtrude","CAP_FACE",FACE,{"disambiguationData":[OSD([sQuery(id+"F10.wireOp",EDGE,"E62"),sQuery(id+"F10.wireOp",EDGE,"E63"),sQuery(id+"F10.wireOp",EDGE,"E64"),sQuery(id+"F10.wireOp",EDGE,"E65"),sQuery(id+"F10.wireOp",EDGE,"E68.filletArc"),sQuery(id+"F10.wireOp",EDGE,"E69.filletArc"),sQuery(id+"F10.wireOp",EDGE,"E70.filletArc")])],"isStart":false});
            var Q1;
            Q1=makeQuery(id+"F11.opExtrude","CAP_FACE",FACE,{"disambiguationData":[OSD([sQuery(id+"F10.wireOp",EDGE,"E62"),sQuery(id+"F10.wireOp",EDGE,"E63"),sQuery(id+"F10.wireOp",EDGE,"E64"),sQuery(id+"F10.wireOp",EDGE,"E65"),sQuery(id+"F10.wireOp",EDGE,"E68.filletArc"),sQuery(id+"F10.wireOp",EDGE,"E69.filletArc"),sQuery(id+"F10.wireOp",EDGE,"E70.filletArc")])],"isStart":true});
            fillet(context, id + "F12", {"entities" : qUnion([Q0, Q1]), "radius" : 5 * mm, "tangentPropagation" : true, "allowEdgeOverflow" : false});
        }
    });
